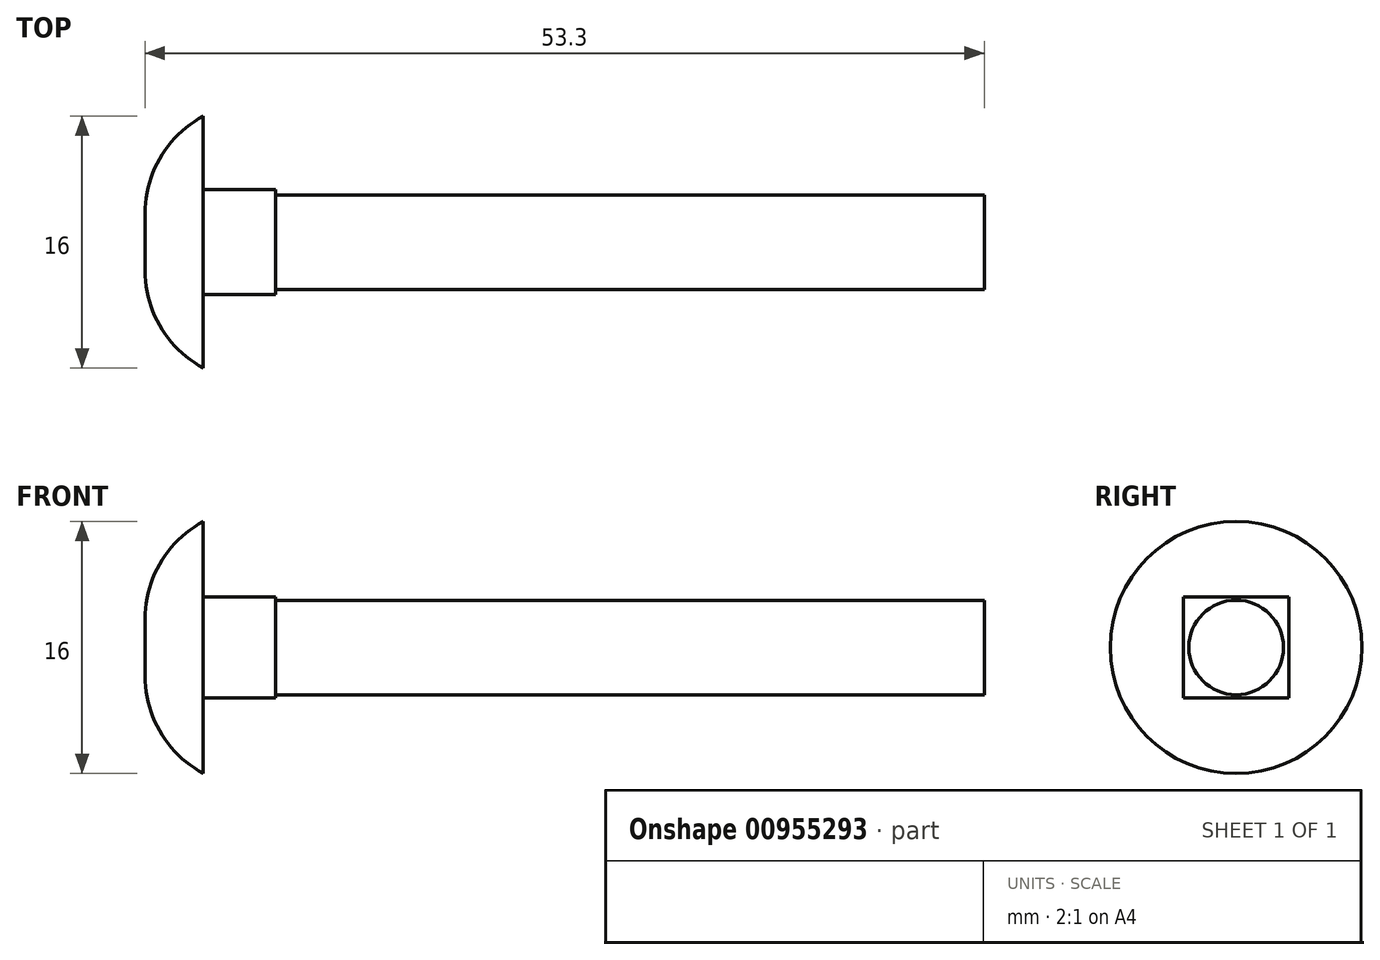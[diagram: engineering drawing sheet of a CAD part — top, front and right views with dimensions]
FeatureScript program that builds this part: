
annotation { "Feature Type Name" : "Feature", "Feature Type Description" : "" }
export const myFeature = defineFeature(function(context is Context, id is Id, definition is map)
    precondition{}
    {
        {
            var Q0;
            Q0=qCreatedBy(makeId("Right.planeOp"),FACE);
            var sketch = newSketch(context, id + "F0", { "sketchPlane" : qUnion([Q0])});
            skCircle(sketch, "E0", {"center": v(0, 0) * mm, "radius": 3 * mm});
            skSolve(sketch);
        }
        {
            var Q0;
            Q0 = qSketchRegion(id + "F0", true);
            extrude(context, id + "F1", {"entities" : qUnion([Q0]), "depth" : 45 * mm, "offsetDistance" : 25 * mm});
        }
        {
            var Q0;
            Q0=makeQuery(id+"F1.opExtrude","CAP_FACE",FACE,{"disambiguationData":[OSD([sQuery(id+"F0.wireOp",EDGE,"E0")])],"isStart":true});
            var sketch = newSketch(context, id + "F2", { "sketchPlane" : qUnion([Q0])});
            skLineSegment(sketch, "E1.bottom", {"start": v(0, 0) * mm, "end": v(-3.35, 0) * mm});
            skLineSegment(sketch, "E1.top", {"start": v(0, 3.2) * mm, "end": v(-3.35, 3.2) * mm});
            skLineSegment(sketch, "E1.left", {"start": v(0, 0) * mm, "end": v(0, 3.2) * mm});
            skLineSegment(sketch, "E1.right", {"start": v(-3.35, 0) * mm, "end": v(-3.35, 3.2) * mm});
            skLineSegment(sketch, "E2.MirrorCS", {"start": v(0, 3.2) * mm, "end": v(3.35, 3.2) * mm});
            skLineSegment(sketch, "E3.MirrorCS", {"start": v(3.35, 0) * mm, "end": v(3.35, 3.2) * mm});
            skLineSegment(sketch, "E4.MirrorCS", {"start": v(0, 0) * mm, "end": v(0, -3.2) * mm});
            skLineSegment(sketch, "E5.MirrorCS", {"start": v(0, -3.2) * mm, "end": v(-3.35, -3.2) * mm});
            skLineSegment(sketch, "E6.MirrorCS", {"start": v(-3.35, 0) * mm, "end": v(-3.35, -3.2) * mm});
            skLineSegment(sketch, "E7.MirrorCS", {"start": v(3.35, 0) * mm, "end": v(3.35, -3.2) * mm});
            skLineSegment(sketch, "E8.MirrorCS", {"start": v(0, -3.2) * mm, "end": v(3.35, -3.2) * mm});
            skSolve(sketch);
        }
        {
            var Q0;
            Q0 = qSketchRegion(id + "F2", true);
            extrude(context, id + "F3", {"entities" : qUnion([Q0]), "operationType" : NewBodyOperationType.ADD, "depth" : 4.6 * mm, "offsetDistance" : 25 * mm});
        }
        {
            var Q0;
            Q0=makeQuery(id+"F3.opExtrude","CAP_FACE",FACE,{"disambiguationData":[OSD([sQuery(id+"F2.wireOp",EDGE,"E1.top"),sQuery(id+"F2.wireOp",EDGE,"E1.right"),sQuery(id+"F2.wireOp",EDGE,"E2.MirrorCS"),sQuery(id+"F2.wireOp",EDGE,"E3.MirrorCS"),sQuery(id+"F2.wireOp",EDGE,"E5.MirrorCS"),sQuery(id+"F2.wireOp",EDGE,"E6.MirrorCS"),sQuery(id+"F2.wireOp",EDGE,"E7.MirrorCS"),sQuery(id+"F2.wireOp",EDGE,"E8.MirrorCS")])],"isStart":false});
            var sketch = newSketch(context, id + "F4", { "sketchPlane" : qUnion([Q0])});
            skCircle(sketch, "E9", {"center": v(0, 0) * mm, "radius": 8 * mm});
            skSolve(sketch);
        }
        {
            var Q0;
            Q0 = qSketchRegion(id + "F4", true);
            extrude(context, id + "F5", {"entities" : qUnion([Q0]), "operationType" : NewBodyOperationType.ADD, "depth" : 3.7 * mm, "offsetDistance" : 25 * mm});
        }
        {
            var Q0;
            Q0=makeQuery(id+"F5.opExtrude","CAP_EDGE",EDGE,{"disambiguationData":[OSD([sQuery(id+"F4.wireOp",EDGE,"E9")])],"isStart":false});
            fillet(context, id + "F6", {"entities" : qUnion([Q0]), "radius" : 7 * mm, "tangentPropagation" : true, "allowEdgeOverflow" : false});
        }
    });
